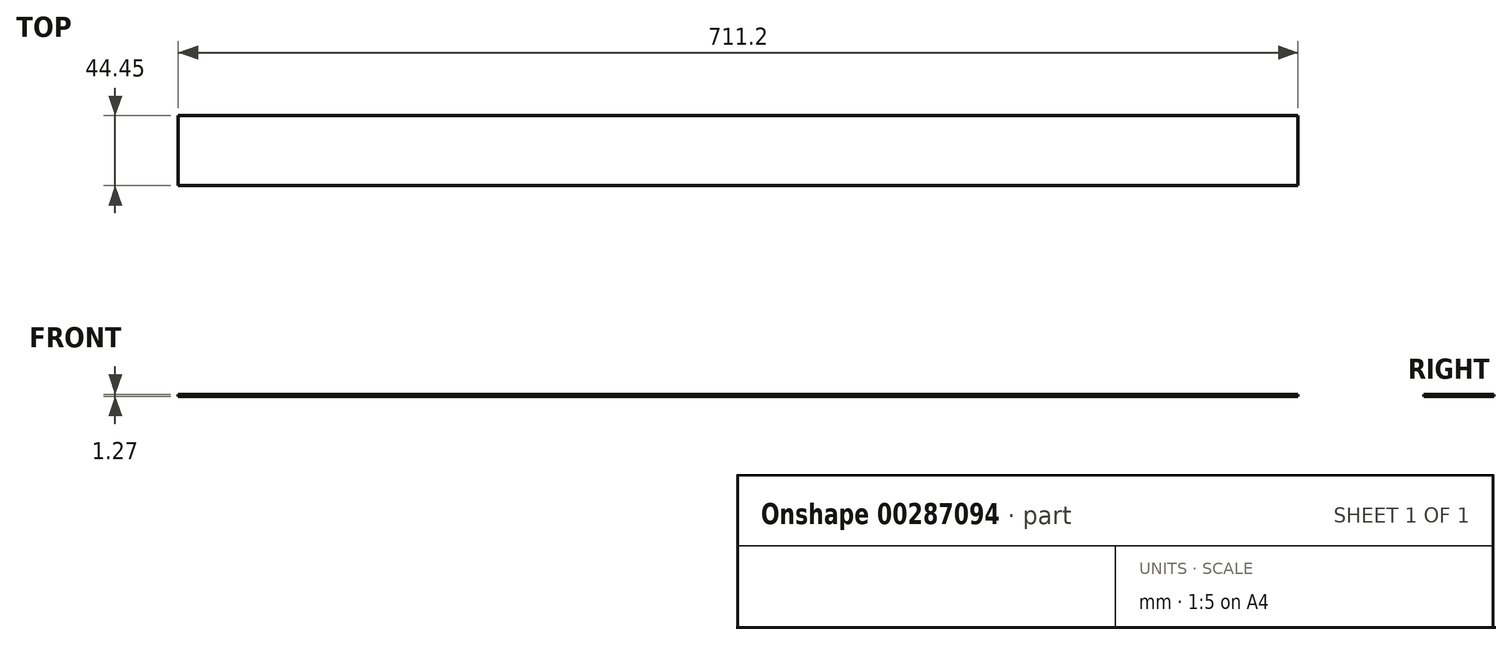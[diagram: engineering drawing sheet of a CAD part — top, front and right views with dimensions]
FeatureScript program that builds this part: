
annotation { "Feature Type Name" : "Feature", "Feature Type Description" : "" }
export const myFeature = defineFeature(function(context is Context, id is Id, definition is map)
    precondition{}
    {
        {
            var Q0;
            Q0=qCreatedBy(makeId("Top.planeOp"),FACE);
            var sketch = newSketch(context, id + "F0", { "sketchPlane" : qUnion([Q0])});
            skLineSegment(sketch, "E0.bottom", {"start": v(-355.6, -157.3) * mm, "end": v(355.6, -157.3) * mm});
            skLineSegment(sketch, "E0.top", {"start": v(-355.6, -201.75) * mm, "end": v(355.6, -201.75) * mm});
            skLineSegment(sketch, "E0.left", {"start": v(-355.6, -157.3) * mm, "end": v(-355.6, -201.75) * mm});
            skLineSegment(sketch, "E0.right", {"start": v(355.6, -157.3) * mm, "end": v(355.6, -201.75) * mm});
            skSolve(sketch);
        }
        {
            var Q0;
            Q0 = qSketchRegion(id + "F0", true);
            extrude(context, id + "F1", {"entities" : qUnion([Q0]), "depth" : 1.27 * mm});
        }
    });
